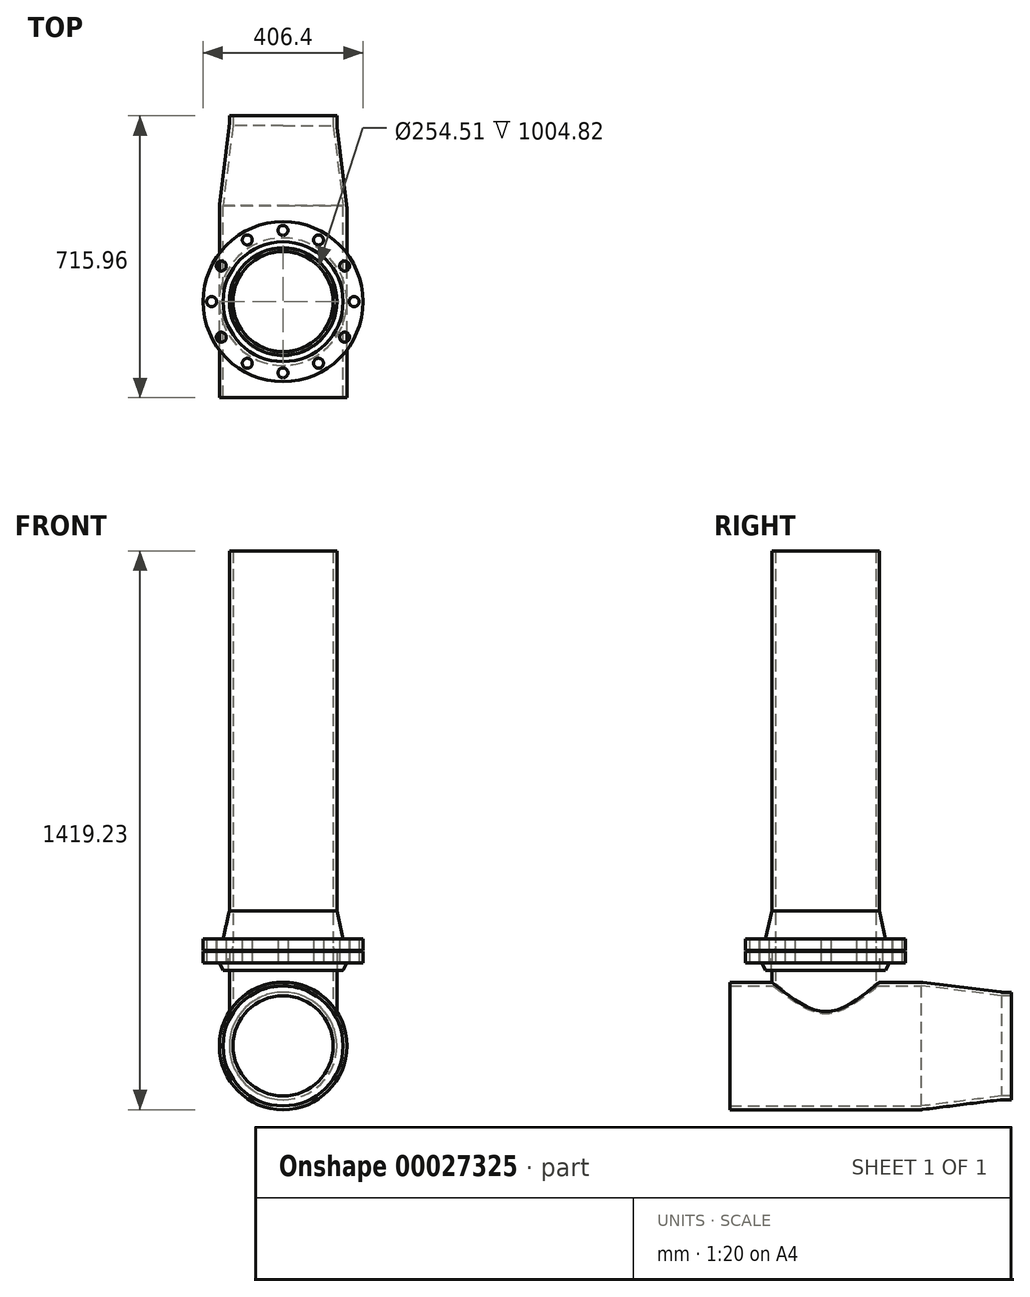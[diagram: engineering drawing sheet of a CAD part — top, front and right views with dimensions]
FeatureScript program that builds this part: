
annotation { "Feature Type Name" : "Feature", "Feature Type Description" : "" }
export const myFeature = defineFeature(function(context is Context, id is Id, definition is map)
    precondition{}
    {
        {
            var Q0;
            Q0=qCreatedBy(makeId("Front.planeOp"),FACE);
            var sketch = newSketch(context, id + "F0", { "sketchPlane" : qUnion([Q0])});
            skLineSegment(sketch, "E0", {"start": v(-161.93, 0) * mm, "end": v(-161.93, 1.59) * mm});
            skLineSegment(sketch, "E1", {"start": v(-161.93, 1.59) * mm, "end": v(-203.2, 1.59) * mm});
            skLineSegment(sketch, "E2", {"start": v(-203.2, 1.59) * mm, "end": v(-203.2, 30.23) * mm});
            skLineSegment(sketch, "E3", {"start": v(-203.2, 30.23) * mm, "end": v(-152.4, 30.23) * mm});
            skLineSegment(sketch, "E4", {"start": v(-152.4, 30.23) * mm, "end": v(-136.52, 101.6) * mm});
            skLineSegment(sketch, "E5", {"start": v(-136.53, 101.6) * mm, "end": v(-127.25, 101.6) * mm});
            skLineSegment(sketch, "E6", {"start": v(-127.25, 101.6) * mm, "end": v(-127.25, 0) * mm});
            skLineSegment(sketch, "E7", {"start": v(-127.25, 0) * mm, "end": v(-161.93, 0) * mm});
            skLineSegment(sketch, "E8", {"start": v(0, 0) * mm, "end": v(0, 81.83) * mm, "construction": true});
            skSolve(sketch);
        }
        {
            var Q0;
            Q0=makeQuery(id+"F0.imprint","IMPRINT",FACE,{"disambiguationData":[TD([[makeQuery(id+"F0.imprint","IMPRINT",EDGE,{"derivedFrom":sQuery(id+"F0.wireOp",EDGE,"E0")}),-1.0]])]});
            var Q1;
            Q1=sQuery(id+"F0.wireOp",EDGE,"E8");
            revolve(context, id + "F1", {"entities" : qUnion([Q0]), "axis" : qUnion([Q1]), "revolveType" : RevolveType.FULL});
        }
        {
            var Q0;
            Q0=makeQuery(id+"F1.opRevolve","SWEPT_FACE",FACE,{"disambiguationData":[OSD([sQuery(id+"F0.wireOp",EDGE,"E1")])]});
            var sketch = newSketch(context, id + "F2", { "sketchPlane" : qUnion([Q0])});
            skCircle(sketch, "E9", {"center": v(0, 0) * mm, "radius": 180.98 * mm, "construction": true});
            skCircle(sketch, "E10", {"center": v(-156.73, -90.49) * mm, "radius": 12.7 * mm});
            skCircle(sketch, "E11.1.0", {"center": v(-180.98, 0) * mm, "radius": 12.7 * mm});
            skCircle(sketch, "E11.2.0", {"center": v(-156.73, 90.49) * mm, "radius": 12.7 * mm});
            skCircle(sketch, "E11.3.0", {"center": v(-90.49, 156.73) * mm, "radius": 12.7 * mm});
            skCircle(sketch, "E11.4.0", {"center": v(0, 180.98) * mm, "radius": 12.7 * mm});
            skCircle(sketch, "E11.5.0", {"center": v(90.49, 156.73) * mm, "radius": 12.7 * mm});
            skCircle(sketch, "E11.6.0", {"center": v(156.73, 90.49) * mm, "radius": 12.7 * mm});
            skCircle(sketch, "E11.7.0", {"center": v(180.98, 0) * mm, "radius": 12.7 * mm});
            skLineSegment(sketch, "E11.anchor1", {"start": v(0, 0) * mm, "end": v(-156.73, -90.49) * mm, "construction": true});
            skLineSegment(sketch, "E11.anchor2", {"start": v(0, 0) * mm, "end": v(-90.49, -156.73) * mm, "construction": true});
            skCircle(sketch, "E12.1.8.0", {"center": v(156.73, -90.49) * mm, "radius": 12.7 * mm});
            skCircle(sketch, "E12.1.9.0", {"center": v(90.49, -156.73) * mm, "radius": 12.7 * mm});
            skCircle(sketch, "E12.1.10.0", {"center": v(0, -180.98) * mm, "radius": 12.7 * mm});
            skCircle(sketch, "E12.1.11.0", {"center": v(-90.49, -156.73) * mm, "radius": 12.7 * mm});
            skSolve(sketch);
        }
        {
            var Q0;
            Q0=sQuery(id+"F2.wireOp",VERTEX,"E11.3.0.center");
            var Q1;
            Q1=sQuery(id+"F2.wireOp",VERTEX,"E11.2.0.center");
            var Q2;
            Q2=sQuery(id+"F2.wireOp",VERTEX,"E11.4.0.center");
            var Q3;
            Q3=sQuery(id+"F2.wireOp",VERTEX,"E11.5.0.center");
            var Q4;
            Q4=sQuery(id+"F2.wireOp",VERTEX,"E11.6.0.center");
            var Q5;
            Q5=sQuery(id+"F2.wireOp",VERTEX,"E11.anchor2.end");
            var Q6;
            Q6=sQuery(id+"F2.wireOp",VERTEX,"E10.center");
            var Q7;
            Q7=sQuery(id+"F2.wireOp",VERTEX,"E11.1.0.center");
            var Q8;
            Q8=sQuery(id+"F2.wireOp",VERTEX,"E12.1.8.0.center");
            var Q9;
            Q9=sQuery(id+"F2.wireOp",VERTEX,"E11.7.0.center");
            var Q10;
            Q10=sQuery(id+"F2.wireOp",VERTEX,"E12.1.9.0.center");
            var Q11;
            Q11=sQuery(id+"F2.wireOp",VERTEX,"E12.1.10.0.center");
            var Q12;
            Q12=makeQuery(id+"F1.opRevolve","SWEPT_BODY",BODY,{"disambiguationData":[OSD([sQuery(id+"F0.wireOp",EDGE,"E0"),sQuery(id+"F0.wireOp",EDGE,"E1"),sQuery(id+"F0.wireOp",EDGE,"E2"),sQuery(id+"F0.wireOp",EDGE,"E3"),sQuery(id+"F0.wireOp",EDGE,"E4"),sQuery(id+"F0.wireOp",EDGE,"E5"),sQuery(id+"F0.wireOp",EDGE,"E6"),sQuery(id+"F0.wireOp",EDGE,"E7")])]});
            hole(context, id + "F3", {"style" : HoleStyle.SIMPLE, "holeDiameter" : 19.05 * mm, "endStyle" : HoleEndStyle.THROUGH, "locations" : qUnion([Q0, Q1, Q2, Q3, Q4, Q5, Q6, Q7, Q8, Q9, Q10, Q11]), "scope" : qUnion([Q12])});
        }
        {
            var Q0;
            Q0=makeQuery(id+"F1.opRevolve","SWEPT_EDGE",EDGE,{"disambiguationData":[OSD([sQuery(id+"F0.wireOp",EDGE,"E6"),sQuery(id+"F0.wireOp",EDGE,"E7")])]});
            fillet(context, id + "F4", {"entities" : qUnion([Q0]), "radius" : 11.18 * mm, "tangentPropagation" : true, "allowEdgeOverflow" : false});
        }
        {
            var Q0;
            Q0=makeQuery(id+"F1.opRevolve","SWEPT_FACE",FACE,{"disambiguationData":[OSD([sQuery(id+"F0.wireOp",EDGE,"E5")])]});
            extrude(context, id + "F5", {"entities" : qUnion([Q0]), "operationType" : NewBodyOperationType.ADD, "depth" : 914.4 * mm});
        }
        {
            var Q0;
            Q0=qCreatedBy(makeId("Front.planeOp"),FACE);
            var sketch = newSketch(context, id + "F6", { "sketchPlane" : qUnion([Q0])});
            skLineSegment(sketch, "E13", {"start": v(161.93, 0) * mm, "end": v(161.93, -1.59) * mm});
            skLineSegment(sketch, "E14", {"start": v(161.93, -1.59) * mm, "end": v(203.2, -1.59) * mm});
            skLineSegment(sketch, "E15", {"start": v(203.2, -1.59) * mm, "end": v(203.2, -30.23) * mm});
            skLineSegment(sketch, "E16", {"start": v(203.2, -30.23) * mm, "end": v(161.93, -30.23) * mm});
            skLineSegment(sketch, "E17", {"start": v(161.92, -30.23) * mm, "end": v(152.4, -49.28) * mm});
            skLineSegment(sketch, "E18", {"start": v(152.4, -49.28) * mm, "end": v(138.18, -49.28) * mm});
            skLineSegment(sketch, "E19", {"start": v(138.18, -49.28) * mm, "end": v(138.18, 0) * mm});
            skLineSegment(sketch, "E20", {"start": v(138.18, 0) * mm, "end": v(161.93, 0) * mm});
            skLineSegment(sketch, "E21", {"start": v(0, -4.02) * mm, "end": v(0, -36.46) * mm});
            skSolve(sketch);
        }
        {
            var Q0;
            Q0=makeQuery(id+"F6.imprint","IMPRINT",FACE,{"disambiguationData":[TD([[makeQuery(id+"F6.imprint","IMPRINT",EDGE,{"derivedFrom":sQuery(id+"F6.wireOp",EDGE,"E13")}),-1.0]])]});
            var Q1;
            Q1=sQuery(id+"F6.wireOp",EDGE,"E21");
            revolve(context, id + "F7", {"operationType" : NewBodyOperationType.ADD, "entities" : qUnion([Q0]), "axis" : qUnion([Q1]), "revolveType" : RevolveType.FULL});
        }
        {
            var Q0;
            Q0=makeQuery(id+"F7.opRevolve","SWEPT_FACE",FACE,{"disambiguationData":[OSD([sQuery(id+"F6.wireOp",EDGE,"E16")])]});
            var sketch = newSketch(context, id + "F8", { "sketchPlane" : qUnion([Q0])});
            skCircle(sketch, "E22", {"center": v(-0.4, -0.16) * mm, "radius": 180.98 * mm, "construction": true});
            skCircle(sketch, "E23", {"center": v(-157.13, -90.65) * mm, "radius": 12.7 * mm});
            skCircle(sketch, "E24.1.0", {"center": v(-181.37, -0.16) * mm, "radius": 12.7 * mm});
            skCircle(sketch, "E24.2.0", {"center": v(-157.13, 90.33) * mm, "radius": 12.7 * mm});
            skCircle(sketch, "E24.3.0", {"center": v(-90.89, 156.57) * mm, "radius": 12.7 * mm});
            skCircle(sketch, "E24.4.0", {"center": v(-0.4, 180.81) * mm, "radius": 12.7 * mm});
            skCircle(sketch, "E24.5.0", {"center": v(90.09, 156.57) * mm, "radius": 12.7 * mm});
            skCircle(sketch, "E24.6.0", {"center": v(156.33, 90.33) * mm, "radius": 12.7 * mm});
            skCircle(sketch, "E24.7.0", {"center": v(180.58, -0.16) * mm, "radius": 12.7 * mm});
            skLineSegment(sketch, "E24.anchor1", {"start": v(-0.4, -0.16) * mm, "end": v(-157.13, -90.65) * mm, "construction": true});
            skLineSegment(sketch, "E24.anchor2", {"start": v(-0.4, -0.16) * mm, "end": v(-90.89, -156.89) * mm, "construction": true});
            skCircle(sketch, "E25.1.8.0", {"center": v(156.33, -90.65) * mm, "radius": 12.7 * mm});
            skCircle(sketch, "E25.1.9.0", {"center": v(90.09, -156.89) * mm, "radius": 12.7 * mm});
            skCircle(sketch, "E25.1.10.0", {"center": v(-0.4, -181.14) * mm, "radius": 12.7 * mm});
            skCircle(sketch, "E25.1.11.0", {"center": v(-90.89, -156.89) * mm, "radius": 12.7 * mm});
            skSolve(sketch);
        }
        {
            var Q0;
            Q0=sQuery(id+"F8.wireOp",VERTEX,"E25.1.8.0.center");
            var Q1;
            Q1=sQuery(id+"F8.wireOp",VERTEX,"E25.1.9.0.center");
            var Q2;
            Q2=sQuery(id+"F8.wireOp",VERTEX,"E25.1.10.0.center");
            var Q3;
            Q3=sQuery(id+"F8.wireOp",VERTEX,"E24.anchor2.end");
            var Q4;
            Q4=sQuery(id+"F8.wireOp",VERTEX,"E23.center");
            var Q5;
            Q5=sQuery(id+"F8.wireOp",VERTEX,"E24.2.0.center");
            var Q6;
            Q6=sQuery(id+"F8.wireOp",VERTEX,"E24.3.0.center");
            var Q7;
            Q7=sQuery(id+"F8.wireOp",VERTEX,"E24.4.0.center");
            var Q8;
            Q8=sQuery(id+"F8.wireOp",VERTEX,"E24.6.0.center");
            var Q9;
            Q9=sQuery(id+"F8.wireOp",VERTEX,"E24.7.0.center");
            var Q10;
            Q10=sQuery(id+"F8.wireOp",VERTEX,"E24.1.0.center");
            var Q11;
            Q11=sQuery(id+"F8.wireOp",VERTEX,"E24.5.0.center");
            var Q12;
            Q12=makeQuery(id+"F1.opRevolve","SWEPT_BODY",BODY,{"disambiguationData":[OSD([sQuery(id+"F0.wireOp",EDGE,"E0"),sQuery(id+"F0.wireOp",EDGE,"E1"),sQuery(id+"F0.wireOp",EDGE,"E2"),sQuery(id+"F0.wireOp",EDGE,"E3"),sQuery(id+"F0.wireOp",EDGE,"E4"),sQuery(id+"F0.wireOp",EDGE,"E5"),sQuery(id+"F0.wireOp",EDGE,"E6"),sQuery(id+"F0.wireOp",EDGE,"E7")])]});
            hole(context, id + "F9", {"style" : HoleStyle.SIMPLE, "holeDiameter" : 25.4 * mm, "endStyle" : HoleEndStyle.THROUGH, "locations" : qUnion([Q0, Q1, Q2, Q3, Q4, Q5, Q6, Q7, Q8, Q9, Q10, Q11]), "scope" : qUnion([Q12])});
        }
        {
            var Q0;
            Q0=makeQuery(id+"F7.opRevolve","SWEPT_FACE",FACE,{"disambiguationData":[OSD([sQuery(id+"F6.wireOp",EDGE,"E18")])]});
            var sketch = newSketch(context, id + "F10", { "sketchPlane" : qUnion([Q0])});
            skCircle(sketch, "E26", {"center": v(0, 0) * mm, "radius": 136.53 * mm});
            skCircle(sketch, "E27", {"center": v(0, 0) * mm, "radius": 127.25 * mm});
            skSolve(sketch);
        }
        {
            var Q0;
            Q0 = qSketchRegion(id + "F10", true);
            extrude(context, id + "F11", {"entities" : qUnion([Q0]), "oppositeDirection" : true, "depth" : 49.28 * mm, "hasSecondDirection" : true, "secondDirectionOppositeDirection" : false, "secondDirectionDepth" : 203.2 * mm});
        }
        {
            var Q0;
            Q0=qCreatedBy(makeId("Front.planeOp"),FACE);
            var sketch = newSketch(context, id + "F12", { "sketchPlane" : qUnion([Q0])});
            skLineSegment(sketch, "E28", {"start": v(0, 0) * mm, "end": v(0, -241.3) * mm});
            skCircle(sketch, "E29", {"center": v(0, -241.3) * mm, "radius": 161.93 * mm});
            skCircle(sketch, "E30", {"center": v(0, -241.3) * mm, "radius": 152.4 * mm});
            skSolve(sketch);
        }
        {
            var Q0;
            Q0=makeQuery(id+"F12.imprint","IMPRINT",FACE,{"disambiguationData":[TD([[makeQuery(id+"F12.imprint","IMPRINT",EDGE,{"derivedFrom":sQuery(id+"F12.wireOp",EDGE,"E29")}),1.0]])]});
            extrude(context, id + "F13", {"entities" : qUnion([Q0]), "operationType" : NewBodyOperationType.ADD, "endBound" : BoundingType.SYMMETRIC, "depth" : 487.36 * mm});
        }
        {
            var Q0;
            Q0=qCreatedBy(makeId("Front.planeOp"),FACE);
            var sketch = newSketch(context, id + "F14", { "sketchPlane" : qUnion([Q0])});
            skCircle(sketch, "E31", {"center": v(0, -241.3) * mm, "radius": 152.4 * mm});
            skSolve(sketch);
        }
        {
            var Q0;
            Q0 = qSketchRegion(id + "F14", true);
            var Q1;
            Q1=makeQuery(id+"F11.opExtrude","SWEPT_BODY",BODY,{"disambiguationData":[OSD([sQuery(id+"F10.wireOp",EDGE,"E26"),sQuery(id+"F10.wireOp",EDGE,"E27")])]});
            var Q2;
            Q2=makeQuery(id+"F11.opExtrude","SWEPT_BODY",BODY,{"disambiguationData":[OSD([sQuery(id+"F10.wireOp",EDGE,"E26"),sQuery(id+"F10.wireOp",EDGE,"E27")])]});
            extrude(context, id + "F15", {"entities" : qUnion([Q0]), "operationType" : NewBodyOperationType.REMOVE, "endBound" : BoundingType.SYMMETRIC, "endBoundEntityBody" : qUnion([Q1]), "depth" : 508 * mm});
        }
        {
            var Q0;
            {var subQ0=sQuery(id+"F6.wireOp",EDGE,"E18");Q0=makeQuery(id+"F10.imprint","IMPRINT",FACE,{"disambiguationData":[TD([[makeQuery(id+"F10.imprint","IMPRINT",EDGE,{"derivedFrom":makeQuery(id+"F7.opRevolve","SWEPT_EDGE",EDGE,{"disambiguationData":[OSD([sQuery(id+"F6.wireOp",EDGE,"E17"),subQ0])]})}),-1.0]])]});}
            var sketch = newSketch(context, id + "F16", { "sketchPlane" : qUnion([Q0])});
            skCircle(sketch, "E32", {"center": v(0, 0) * mm, "radius": 127.25 * mm});
            skSolve(sketch);
        }
        {
            var Q0;
            Q0 = qSketchRegion(id + "F16", true);
            extrude(context, id + "F17", {"entities" : qUnion([Q0]), "operationType" : NewBodyOperationType.REMOVE, "depth" : 203.2 * mm});
        }
        {
            var Q0;
            {var subQ0=sQuery(id+"F12.wireOp",EDGE,"E30");var subQ1=makeQuery(id+"F13.opExtrude","SWEPT_FACE",FACE,{"disambiguationData":[OSD([subQ0])]});Q0=makeQuery(id+"F17.boolean.opBoolean","INTERSECT",EDGE,{"derivedFrom":[makeQuery(id+"F15.boolean.opBoolean","MERGE",FACE,{"derivedFrom":[makeQuery(id+"F13.boolean.opBoolean","SPLIT",FACE,{"disambiguationData":[TD([makeQuery(id+"F11.opExtrude","SWEPT_FACE",FACE,{"disambiguationData":[OSD([sQuery(id+"F10.wireOp",EDGE,"E27")])]})])],"derivedFrom":subQ1}),makeQuery(id+"F13.boolean.opBoolean","SPLIT",FACE,{"disambiguationData":[TD([makeQuery(id+"F11.opExtrude","SWEPT_FACE",FACE,{"disambiguationData":[OSD([sQuery(id+"F10.wireOp",EDGE,"E26")])]})])],"derivedFrom":subQ1}),makeQuery(id+"F15.opExtrude","SWEPT_FACE",FACE,{"disambiguationData":[OSD([sQuery(id+"F14.wireOp",EDGE,"E31")])]})]}),makeQuery(id+"F17.opExtrude","SWEPT_FACE",FACE,{"disambiguationData":[OSD([sQuery(id+"F16.wireOp",EDGE,"E32")])]})]});}
            fillet(context, id + "F18", {"entities" : qUnion([Q0]), "radius" : 5.08 * mm, "tangentPropagation" : true, "allowEdgeOverflow" : false});
        }
        {
            var Q0;
            Q0=makeQuery(id+"F13.opExtrude","CAP_FACE",FACE,{"disambiguationData":[OSD([sQuery(id+"F12.wireOp",EDGE,"E29"),sQuery(id+"F12.wireOp",EDGE,"E30")])],"isStart":true});
            var sketch = newSketch(context, id + "F19", { "sketchPlane" : qUnion([Q0])});
            skCircle(sketch, "E33", {"center": v(0, -241.3) * mm, "radius": 127.25 * mm});
            skCircle(sketch, "E34", {"center": v(0, -241.3) * mm, "radius": 136.53 * mm});
            skSolve(sketch);
        }
        {
            var Q0;
            Q0 = qSketchRegion(id + "F19", true);
            extrude(context, id + "F20", {"entities" : qUnion([Q0]), "depth" : 228.6 * mm, "hasSecondDirection" : true, "secondDirectionOppositeDirection" : false, "secondDirectionDepth" : 203.2 * mm});
        }
        {
            var Q0;
            Q0=makeQuery(id+"F13.opExtrude","CAP_FACE",FACE,{"disambiguationData":[OSD([sQuery(id+"F12.wireOp",EDGE,"E29"),sQuery(id+"F12.wireOp",EDGE,"E30")])],"isStart":true});
            var sketch = newSketch(context, id + "F21", { "sketchPlane" : qUnion([Q0])});
            skPoint(sketch, "E35", {"position": v(0, -241.3) * mm});
            skLineSegment(sketch, "E36", {"start": v(0, -241.3) * mm, "end": v(-152.4, -241.3) * mm, "construction": true});
            skSolve(sketch);
        }
        {
            var Q0;
            Q0=makeQuery(id+"F20.opExtrude","CAP_FACE",FACE,{"disambiguationData":[OSD([sQuery(id+"F19.wireOp",EDGE,"E33"),sQuery(id+"F19.wireOp",EDGE,"E34")])],"isStart":true});
            var sketch = newSketch(context, id + "F22", { "sketchPlane" : qUnion([Q0])});
            skPoint(sketch, "E37", {"position": v(0, -241.3) * mm});
            skSolve(sketch);
        }
        {
            var Q0;
            Q0=sQuery(id+"F21.wireOp",VERTEX,"E36.end");
            var Q1;
            Q1=sQuery(id+"F21.wireOp",VERTEX,"E35");
            var Q2;
            Q2=sQuery(id+"F22.wireOp",VERTEX,"E37");
            cPlane(context, id + "F23", {"entities" : qUnion([Q0, Q1, Q2]), "cplaneType" : CPlaneType.THREE_POINT, "offset" : 152.4 * mm, "width" : 152.4 * mm, "height" : 152.4 * mm});
        }
        {
            var Q0;
            Q0=qCreatedBy(id+"F23.planeOp",FACE);
            var sketch = newSketch(context, id + "F24", { "sketchPlane" : qUnion([Q0])});
            skLineSegment(sketch, "E38", {"start": v(127.25, 446.88) * mm, "end": v(152.65, 243.68) * mm});
            skLineSegment(sketch, "E39", {"start": v(161.93, 243.68) * mm, "end": v(136.52, 446.88) * mm});
            skLineSegment(sketch, "E40", {"start": v(136.52, 446.88) * mm, "end": v(127.25, 446.88) * mm});
            skLineSegment(sketch, "E41", {"start": v(161.93, 243.68) * mm, "end": v(152.65, 243.68) * mm});
            skLineSegment(sketch, "E42", {"start": v(0, 243.94) * mm, "end": v(0, 446.18) * mm, "construction": true});
            skSolve(sketch);
        }
        {
            var Q0;
            Q0=makeQuery(id+"F24.imprint","IMPRINT",FACE,{"disambiguationData":[TD([[makeQuery(id+"F24.imprint","IMPRINT",EDGE,{"derivedFrom":sQuery(id+"F24.wireOp",EDGE,"E38")}),1.0]])]});
            var Q1;
            Q1=sQuery(id+"F24.wireOp",EDGE,"E42");
            revolve(context, id + "F25", {"entities" : qUnion([Q0]), "axis" : qUnion([Q1]), "revolveType" : RevolveType.FULL});
        }
        {
            var Q0;
            Q0=makeQuery(id+"F20.opExtrude","SWEPT_BODY",BODY,{"disambiguationData":[OSD([sQuery(id+"F19.wireOp",EDGE,"E33"),sQuery(id+"F19.wireOp",EDGE,"E34")])]});
            var Q1;
            Q1=makeQuery(id+"F25.opRevolve","SWEPT_BODY",BODY,{"disambiguationData":[OSD([sQuery(id+"F24.wireOp",EDGE,"E38"),sQuery(id+"F24.wireOp",EDGE,"E39"),sQuery(id+"F24.wireOp",EDGE,"E40"),sQuery(id+"F24.wireOp",EDGE,"E41")])]});
            booleanBodies(context, id + "F26", {"operationType" : BooleanOperationType.UNION, "tools" : qUnion([Q0, Q1])});
        }
        {
            var Q0;
            Q0=makeQuery(id+"F11.opExtrude","SWEPT_BODY",BODY,{"disambiguationData":[OSD([sQuery(id+"F10.wireOp",EDGE,"E26"),sQuery(id+"F10.wireOp",EDGE,"E27")])]});
            var Q1;
            Q1=makeQuery(id+"F20.opExtrude","SWEPT_BODY",BODY,{"disambiguationData":[OSD([sQuery(id+"F19.wireOp",EDGE,"E33"),sQuery(id+"F19.wireOp",EDGE,"E34")])]});
            booleanBodies(context, id + "F27", {"operationType" : BooleanOperationType.UNION, "tools" : qUnion([Q0, Q1])});
        }
        {
            var Q0;
            Q0=makeQuery(id+"F27.opBoolean","MERGE",EDGE,{"derivedFrom":[makeQuery(id+"F13.opExtrude","CAP_EDGE",EDGE,{"disambiguationData":[OSD([sQuery(id+"F12.wireOp",EDGE,"E29")])],"isStart":true}),makeQuery(id+"F25.opRevolve","SWEPT_EDGE",EDGE,{"disambiguationData":[OSD([sQuery(id+"F24.wireOp",EDGE,"E39"),sQuery(id+"F24.wireOp",EDGE,"E41")])]})]});
            var Q1;
            Q1=makeQuery(id+"F26.opBoolean","MERGE",EDGE,{"derivedFrom":[makeQuery(id+"F20.opExtrude","CAP_EDGE",EDGE,{"disambiguationData":[OSD([sQuery(id+"F19.wireOp",EDGE,"E34")])],"isStart":true}),makeQuery(id+"F25.opRevolve","SWEPT_EDGE",EDGE,{"disambiguationData":[OSD([sQuery(id+"F24.wireOp",EDGE,"E39"),sQuery(id+"F24.wireOp",EDGE,"E40")])]})]});
            fillet(context, id + "F28", {"entities" : qUnion([Q0, Q1]), "radius" : 50.8 * mm, "tangentPropagation" : true, "allowEdgeOverflow" : false});
        }
    });
